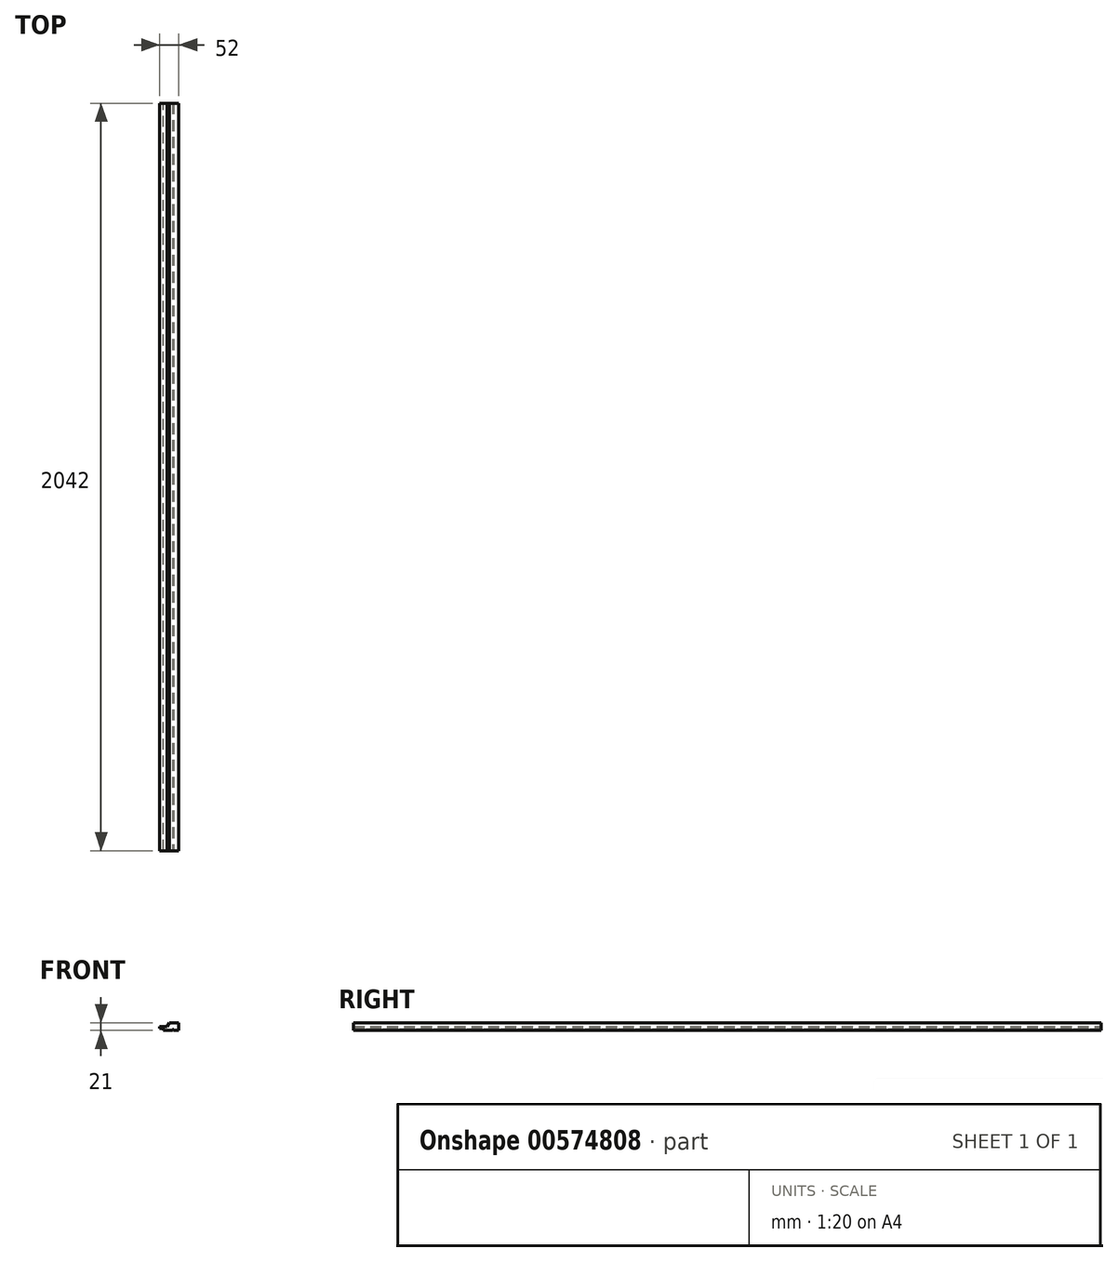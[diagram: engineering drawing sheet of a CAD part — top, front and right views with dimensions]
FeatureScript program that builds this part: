
annotation { "Feature Type Name" : "Feature", "Feature Type Description" : "" }
export const myFeature = defineFeature(function(context is Context, id is Id, definition is map)
    precondition{}
    {
        {
            var Q0;
            Q0=qCreatedBy(makeId("Front.planeOp"),FACE);
            var sketch = newSketch(context, id + "F0", { "sketchPlane" : qUnion([Q0])});
            skLineSegment(sketch, "E0", {"start": v(-21.73, 10.5) * mm, "end": v(47.5, 10.5) * mm});
            skLineSegment(sketch, "E1", {"start": v(47.5, 10.5) * mm, "end": v(47.5, 0.5) * mm});
            skLineSegment(sketch, "E2", {"start": v(47.5, 0.5) * mm, "end": v(37.5, 0.5) * mm});
            skLineSegment(sketch, "E3", {"start": v(37.5, 0.5) * mm, "end": v(37.5, -4.5) * mm});
            skLineSegment(sketch, "E4", {"start": v(37.5, -4.5) * mm, "end": v(47.5, -4.5) * mm});
            skLineSegment(sketch, "E5", {"start": v(47.5, -4.5) * mm, "end": v(47.5, -10.5) * mm});
            skLineSegment(sketch, "E6", {"start": v(47.5, -10.5) * mm, "end": v(-37.5, -10.5) * mm});
            skLineSegment(sketch, "E7", {"start": v(-37.5, -10.5) * mm, "end": v(-37.5, -4.5) * mm});
            skLineSegment(sketch, "E8", {"start": v(-37.5, -4.5) * mm, "end": v(-47.5, -4.5) * mm});
            skLineSegment(sketch, "E9", {"start": v(-47.5, -4.5) * mm, "end": v(-47.5, 0.5) * mm});
            skLineSegment(sketch, "E10", {"start": v(-47.5, 0.5) * mm, "end": v(-27.5, 0.5) * mm});
            skLineSegment(sketch, "E11", {"start": v(-27.5, 0.5) * mm, "end": v(-21.73, 10.5) * mm});
            skSolve(sketch);
        }
        {
            var Q0;
            Q0=qSketchRegion(id+"F0",true);
            extrude(context, id + "F1", {"entities" : qUnion([Q0]), "depth" : 2042 * mm, "offsetDistance" : 25 * mm});
        }
        {
            var Q0;
            Q0=makeQuery(id+"F1.opExtrude","CAP_FACE",FACE,{"disambiguationData":[OSD([sQuery(id+"F0.wireOp",EDGE,"E0"),sQuery(id+"F0.wireOp",EDGE,"E1"),sQuery(id+"F0.wireOp",EDGE,"E2"),sQuery(id+"F0.wireOp",EDGE,"E3"),sQuery(id+"F0.wireOp",EDGE,"E4"),sQuery(id+"F0.wireOp",EDGE,"E5"),sQuery(id+"F0.wireOp",EDGE,"E6"),sQuery(id+"F0.wireOp",EDGE,"E7"),sQuery(id+"F0.wireOp",EDGE,"E8"),sQuery(id+"F0.wireOp",EDGE,"E9"),sQuery(id+"F0.wireOp",EDGE,"E10"),sQuery(id+"F0.wireOp",EDGE,"E11")])],"isStart":false});
            var sketch = newSketch(context, id + "F2", { "sketchPlane" : qUnion([Q0])});
            skLineSegment(sketch, "E12.bottom", {"start": v(-12.5, -10.5) * mm, "end": v(-9.5, -10.5) * mm});
            skLineSegment(sketch, "E12.top", {"start": v(-12.5, -7.5) * mm, "end": v(-9.5, -7.5) * mm});
            skLineSegment(sketch, "E12.left", {"start": v(-12.5, -10.5) * mm, "end": v(-12.5, -7.5) * mm});
            skLineSegment(sketch, "E12.right", {"start": v(-9.5, -10.5) * mm, "end": v(-9.5, -7.5) * mm});
            skLineSegment(sketch, "E13.bottom", {"start": v(47.5, 10.5) * mm, "end": v(4.5, 10.5) * mm});
            skLineSegment(sketch, "E13.top", {"start": v(47.5, -10.5) * mm, "end": v(4.5, -10.5) * mm});
            skLineSegment(sketch, "E13.left", {"start": v(47.5, 10.5) * mm, "end": v(47.5, -10.5) * mm});
            skLineSegment(sketch, "E13.right", {"start": v(4.5, 10.5) * mm, "end": v(4.5, -10.5) * mm});
            skSolve(sketch);
        }
        {
            var Q0;
            Q0=qSketchRegion(id+"F2",true);
            extrude(context, id + "F3", {"entities" : qUnion([Q0]), "operationType" : NewBodyOperationType.REMOVE, "endBound" : BoundingType.THROUGH_ALL, "oppositeDirection" : true, "depth" : 25 * mm, "offsetDistance" : 25 * mm});
        }
    });
